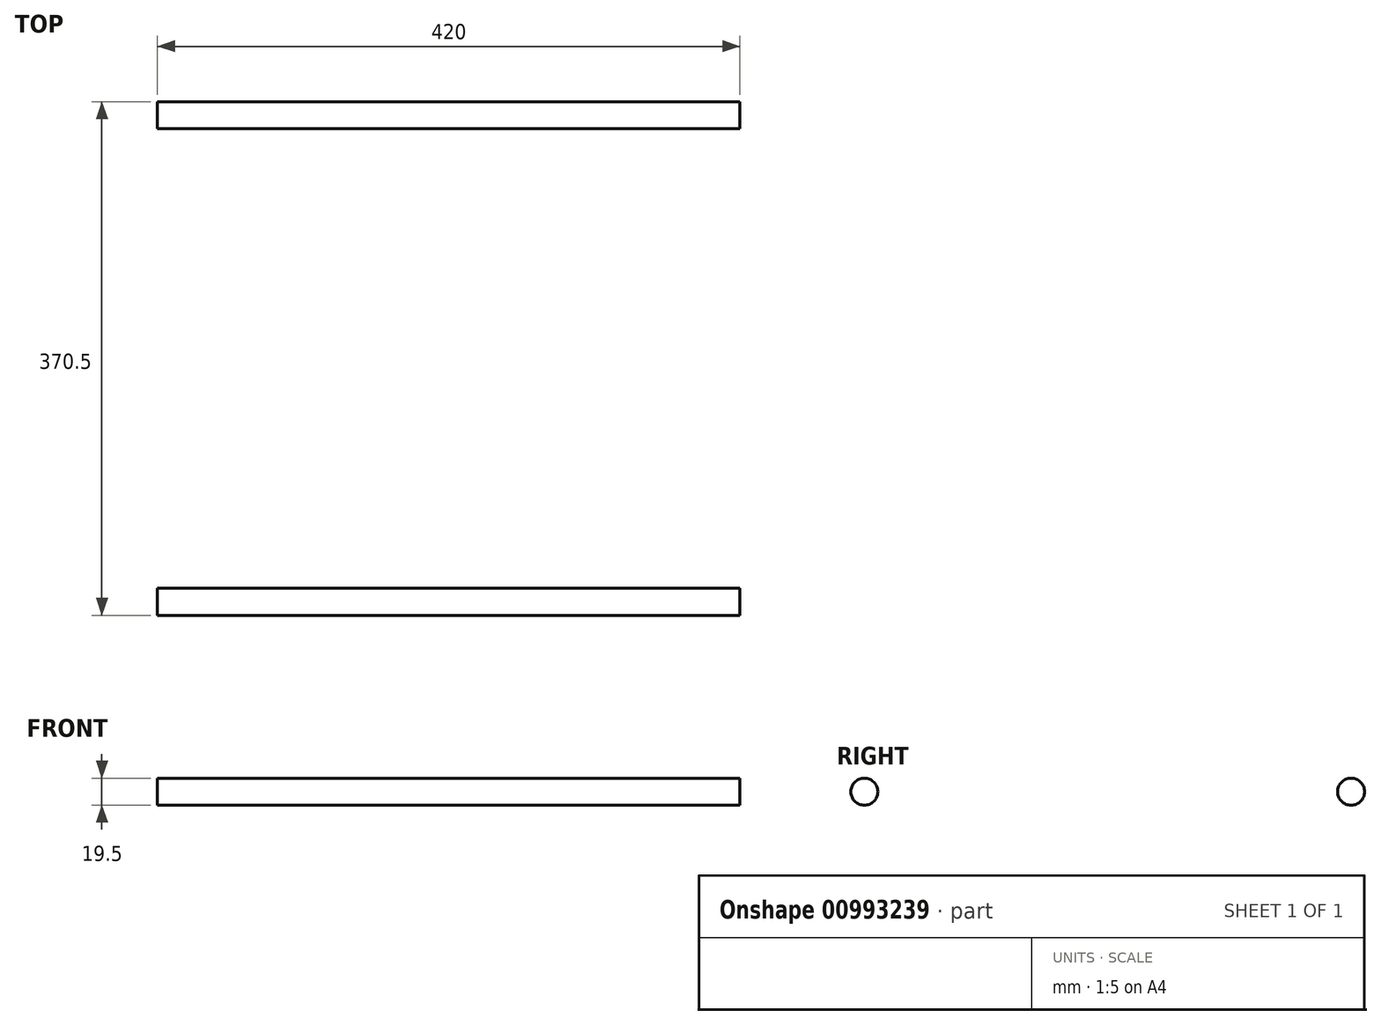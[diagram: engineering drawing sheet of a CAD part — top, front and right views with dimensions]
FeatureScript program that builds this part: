
annotation { "Feature Type Name" : "Feature", "Feature Type Description" : "" }
export const myFeature = defineFeature(function(context is Context, id is Id, definition is map)
    precondition{}
    {
        {
            var Q0;
            Q0=qCreatedBy(makeId("Top.planeOp"),FACE);
            var sketch = newSketch(context, id + "F0", { "sketchPlane" : qUnion([Q0])});
            skLineSegment(sketch, "E0", {"start": v(210, 175.5) * mm, "end": v(-210, 175.5) * mm});
            skSolve(sketch);
        }
        {
            var Q0;
            Q0=qCreatedBy(makeId("Right.planeOp"),FACE);
            var sketch = newSketch(context, id + "F1", { "sketchPlane" : qUnion([Q0])});
            skCircle(sketch, "E1", {"center": v(175.5, 0) * mm, "radius": 9.75 * mm});
            skSolve(sketch);
        }
        {
            var Q0;
            Q0=makeQuery(id+"F1.imprint","IMPRINT",FACE,{"disambiguationData":[TD([[makeQuery(id+"F1.imprint","IMPRINT",EDGE,{"derivedFrom":sQuery(id+"F1.wireOp",EDGE,"E1")}),1.0]])]});
            var Q1;
            Q1=sQuery(id+"F0.wireOp",EDGE,"E0");
            sweep(context, id + "F2", {"profiles" : qUnion([Q0]), "path" : qUnion([Q1])});
        }
        {
            var Q0;
            Q0=makeQuery(id+"F2.opSweep","SWEPT_BODY",BODY,{"disambiguationData":[OSD([sQuery(id+"F0.wireOp",EDGE,"E0"),sQuery(id+"F1.wireOp",EDGE,"E1")])]});
            var Q1;
            Q1=qCreatedBy(makeId("Front.planeOp"),FACE);
            mirror(context, id + "F3", {"entities" : qUnion([Q0]), "mirrorPlane" : qUnion([Q1])});
        }
    });
